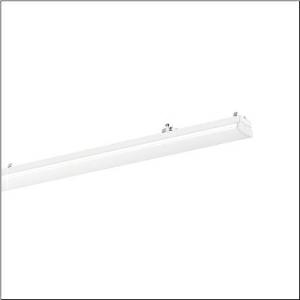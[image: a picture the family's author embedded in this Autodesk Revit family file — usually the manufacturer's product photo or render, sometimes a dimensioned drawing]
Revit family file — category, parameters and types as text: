
# Revit family: licross_11_recessed_opal_mo_51te1ddv495g
name_source: partatom
category: Lighting Fixtures
units: mm (PartAtom-declared; Revit-internal decimal feet)

## family parameters
Cut with Voids When Loaded = No
Host = Face
Light Source = No
Part Type = Normal
Room Calculation Point = No
Round Connector Dimension = Use Diameter
Shared = No

## types (1)
- --- (1 x LED, 9500 lm, 52.6 W, 4000K)
    Apparent Load = 53 VA
    CIE Flux Codes = 44 73 91 87 100
    Color Rendering = 80
    Color Temperature = 4000K
    Default Elevation = 1800 mm
    Description = Licross 11 recessed opal MO, luminaire insert, of sheet steel, coil coated, white, length: 2.250mm, width: 76mm, height: 87mm, LED rated luminous flux: 9.500lm, light colour: 840, SDCM (Standard Deviation of Colour Matching)MacAdam ≤ 2 SDCM (initial), control gear: DALI 2, with plug, 5-pole, with phase selection, mains connection: 220..240V, AC, 50/60Hz, rated input power: 53W, internal wiring halogen-free, primary optical cover: cover, of PMMA, light emission: direct with ceiling illumination distribution, primary light characteristic: symmetric, protection rating (complete): IP54, insulation class (complete): insulation class I (protective earthing), certification: CE, ENEC, VDE, UKCA, protection symbol: D if used in an environment with non-conductive dust loads with corresponding accessories, impact resistance: IK06, permissible ambient temperature for indoor applications: -25..+40°C, corresponds to IFS (International Featured Standards) requirements for safety and quality in the food industry, reducing of maximum allowable ambient temperature of 5°C with ceiling mounting, LABS conformity tested according to VDMA 24364:2018-05, The light source and the operating device comply with the requirements of the Ecodesign Regulation (EU) 2019/2020 and are replaceable in accordance with this regulation, packaging unit: 1 piece
    Height = 83 mm
    Lamp = 1 x LED
    Lamp Light Flux = 9500 lm
    Lamp Power = 52.6 W
    Lamp count = 1
    Length = 2250 mm
    Luminous efficacy = 181 lm/W
    Manufacturer = Siteco
    ModVariant = No
    Model = 51TE1DDV495G
    Mounting Place = Ceiling
    Mounting Type = Pendant
    Number of Poles = 1
    OnlyDefault = Yes
    Power Factor = 1
    Product Name = Licross 11 recessed opal MO
    Product group = luminaire insert | ceiling pendant
    ProductGroupID = 901
    Protection Class = Protection class I
    Protection Degree = IP 54
    RLX_Detail_Level = 1
    RLX_Emergency_Light_Flux = 0 lm
    RLX_Emergency_Type = 0
    RLX_Emergency_Type_DB = No
    RlxData = <blob elided: 26697 chars, md5=fc8c174a>
    Socket = socket
    Standby Power = 0 W
    System Light Flux = 9500 lm
    System Power = 53 W
    Type Comments = factory setting: luminous flux: 100 % | dim-lin: 254 | 239 mA
    Type Image = l_1313666.jpg
    URL = http://relux.com
    VarID = @adj_084129
    Voltage = 0 V
    Weight = 0.00 kg
    Width = 76 mm

## geometry (parser evidence)
native form markers: Blend x4, Sweep x13
no freeform markers — native parametric forms only
